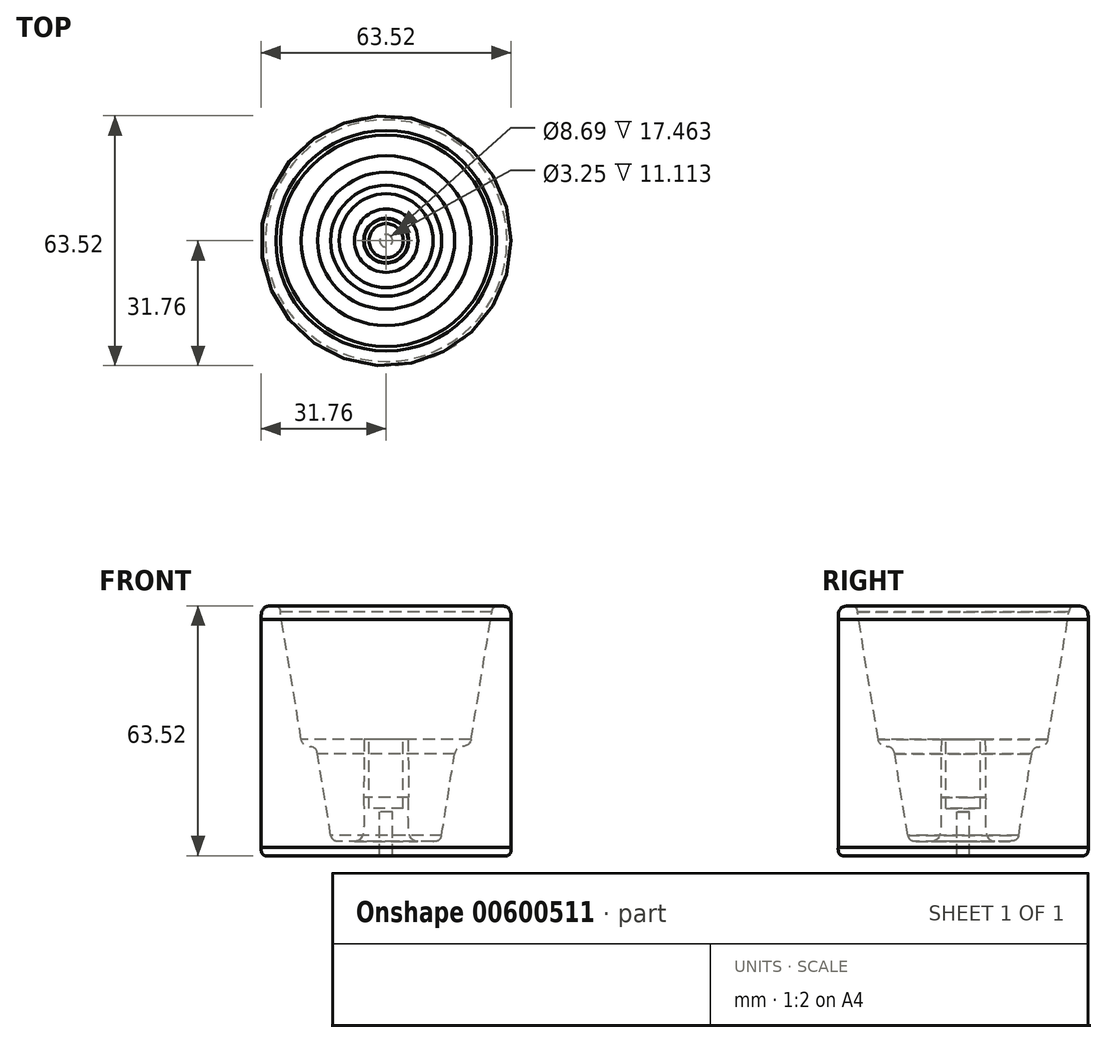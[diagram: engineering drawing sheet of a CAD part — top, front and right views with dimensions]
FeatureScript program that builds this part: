
annotation { "Feature Type Name" : "Feature", "Feature Type Description" : "" }
export const myFeature = defineFeature(function(context is Context, id is Id, definition is map)
    precondition{}
    {
        {
            var Q0;
            Q0=qCreatedBy(makeId("Front.planeOp"),FACE);
            var sketch = newSketch(context, id + "F0", { "sketchPlane" : qUnion([Q0])});
            skLineSegment(sketch, "E0", {"start": v(0, 0) * mm, "end": v(1.63, 0) * mm});
            skLineSegment(sketch, "E1", {"start": v(1.63, 0) * mm, "end": v(1.63, -11.11) * mm});
            skLineSegment(sketch, "E2", {"start": v(5.58, 18.44) * mm, "end": v(4.34, 18.44) * mm});
            skLineSegment(sketch, "E3", {"start": v(4.34, 18.44) * mm, "end": v(4.34, 0.98) * mm});
            skLineSegment(sketch, "E4", {"start": v(4.34, 0.98) * mm, "end": v(0, 0.98) * mm});
            skLineSegment(sketch, "E5", {"start": v(0, 0.98) * mm, "end": v(0, 0) * mm});
            skLineSegment(sketch, "E6", {"start": v(31.75, -8.93) * mm, "end": v(31.75, 48.94) * mm});
            skLineSegment(sketch, "E7", {"start": v(5.58, 18.44) * mm, "end": v(5.7, 3.75) * mm});
            skLineSegment(sketch, "E8", {"start": v(11.92, -7.42) * mm, "end": v(8.06, -7.42) * mm});
            skFitSpline(sketch, "E9", {"points": [v(8.06, -7.42) * mm, v(6.95, -7.14) * mm, v(5.94, -5.7) * mm, v(5.7, 3.75) * mm], "startDerivative": vector(-10.53, -0.3) * mm, "endDerivative": vector(-0.36, 4.47) * mm});
            skLineSegment(sketch, "E10", {"start": v(1.63, -11.11) * mm, "end": v(30.7, -11.11) * mm});
            skFitSpline(sketch, "E11", {"points": [v(30.7, -11.11) * mm, v(31.38, -10.7) * mm, v(31.72, -9.99) * mm, v(31.75, -8.93) * mm], "startDerivative": vector(2.59, 0.9) * mm, "endDerivative": vector(-0.06, 2.95) * mm});
            skFitSpline(sketch, "E12", {"points": [v(31.75, 48.94) * mm, v(31.57, 50.94) * mm, v(30.98, 51.86) * mm, v(28.01, 52.39) * mm], "startDerivative": vector(0.17, 8.36) * mm, "endDerivative": vector(-12.57, -0.66) * mm});
            skFitSpline(sketch, "E13", {"points": [v(26.87, 50.8) * mm, v(27.03, 51.55) * mm, v(27.37, 52.05) * mm, v(28.01, 52.39) * mm], "startDerivative": vector(0.2, 2.28) * mm, "endDerivative": vector(1.8, 0.51) * mm});
            skLineSegment(sketch, "E14", {"start": v(26.87, 50.8) * mm, "end": v(21.57, 18.44) * mm});
            skFitSpline(sketch, "E15", {"points": [v(21.57, 18.44) * mm, v(21.23, 17.53) * mm, v(20.35, 16.93) * mm, v(19.31, 16.62) * mm, v(18.08, 16.18) * mm, v(17.4, 14.82) * mm], "startDerivative": vector(-1.22, -5.41) * mm, "endDerivative": vector(-2.16, -7.01) * mm});
            skLineSegment(sketch, "E16", {"start": v(17.4, 14.82) * mm, "end": v(14.1, -5.96) * mm});
            skFitSpline(sketch, "E17", {"points": [v(11.92, -7.42) * mm, v(12.91, -7.28) * mm, v(13.73, -6.78) * mm, v(14.1, -5.96) * mm], "startDerivative": vector(2.74, 0.69) * mm, "endDerivative": vector(0.89, 2.38) * mm});
            skSolve(sketch);
        }
        {
            var Q0;
            Q0 = qSketchRegion(id + "F0", true);
            var Q1;
            Q1=sQuery(id+"F0.wireOp",EDGE,"E5");
            revolve(context, id + "F1", {"entities" : qUnion([Q0]), "axis" : qUnion([Q1]), "revolveType" : RevolveType.FULL});
        }
        {
            var Q0;
            Q0=makeQuery(id+"F1.opRevolve","SWEPT_FACE",FACE,{"disambiguationData":[OSD([sQuery(id+"F0.wireOp",EDGE,"E4")])]});
            var sketch = newSketch(context, id + "F2", { "sketchPlane" : qUnion([Q0])});
            skCircle(sketch, "E18", {"center": v(0, 0) * mm, "radius": 4.75 * mm});
            skSolve(sketch);
        }
        {
            var Q0;
            Q0 = qSketchRegion(id + "F2", true);
            extrude(context, id + "F3", {"entities" : qUnion([Q0]), "depth" : 9.52 * mm, "offsetDistance" : 25.4 * mm});
        }
        {
            var Q0;
            Q0=makeQuery(id+"F3.opExtrude","SWEPT_BODY",BODY,{"disambiguationData":[OSD([sQuery(id+"F2.wireOp",EDGE,"E18")])]});
            deleteBodies(context, id + "F4", {"entities" : qUnion([Q0])});
        }
        {
            var Q0;
            Q0=makeQuery(id+"F1.opRevolve","SWEPT_BODY",BODY,{"disambiguationData":[OSD([sQuery(id+"F0.wireOp",EDGE,"E0"),sQuery(id+"F0.wireOp",EDGE,"E1"),sQuery(id+"F0.wireOp",EDGE,"E2"),sQuery(id+"F0.wireOp",EDGE,"E3"),sQuery(id+"F0.wireOp",EDGE,"E4"),sQuery(id+"F0.wireOp",EDGE,"E5"),sQuery(id+"F0.wireOp",EDGE,"E6"),sQuery(id+"F0.wireOp",EDGE,"E7"),sQuery(id+"F0.wireOp",EDGE,"E8"),sQuery(id+"F0.wireOp",EDGE,"E9"),sQuery(id+"F0.wireOp",EDGE,"E10"),sQuery(id+"F0.wireOp",EDGE,"E11"),sQuery(id+"F0.wireOp",EDGE,"E12"),sQuery(id+"F0.wireOp",EDGE,"E13"),sQuery(id+"F0.wireOp",EDGE,"E14"),sQuery(id+"F0.wireOp",EDGE,"E15"),sQuery(id+"F0.wireOp",EDGE,"E16"),sQuery(id+"F0.wireOp",EDGE,"E17")])]});
            transform(context, id + "F5", {"entities" : qUnion([Q0]), "transformType" : TransformType.TRANSLATION_3D, "dx" : 0 * mm, "dy" : 0 * mm, "dz" : 11.1 * mm, "makeCopy" : false});
        }
    });
